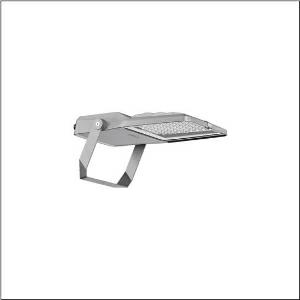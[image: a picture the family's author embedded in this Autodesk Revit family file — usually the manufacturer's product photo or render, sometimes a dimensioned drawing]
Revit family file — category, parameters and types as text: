
# Revit family: floodlight_fl_21_mini___pl64_5xa7776d2e1a_08ea
name_source: partatom
category: Lighting Fixtures
units: mm (PartAtom-declared; Revit-internal decimal feet)

## family parameters
Cut with Voids When Loaded = No
Host = Face
Light Source = No
Part Type = Normal
Room Calculation Point = No
Round Connector Dimension = Use Diameter
Shared = No

## types (1)
- --- (1 x LED, 17220 lm, 142.9 W, 3000K)
    Apparent Load = 143 VA
    CIE Flux Codes = 28 80 98 100 100
    Color Rendering = 70
    Color Temperature = 3000K
    Default Elevation = 1800 mm
    Description = Floodlight FL 21 mini, floodlight, primary light control with lens, of PMMA, primary optical cover: protective disc, of toughened safety glass, transparent, light distribution: PL64, light emission: direct distribution, installation type: surface-mounted, LED, High Power LED, rated luminous flux: 17.220lm, luminous efficacy: 121lm/W, light colour: 730, colour temperature: 3000K, control gear: Smart Interface (Zhaga), control: flexible luminous flux parameterisation, time-dependent luminous flux control, constant luminous flux control, overheat protection, pre-setting: logarithmic dimming characteristic, with terminal, 6-pole, mains connection: 220..240V, AC, 50/60Hz, start of lifetime: 143W, end of service life: 151W, reduction: 63W, luminaire housing, of diecast aluminium, powder-coated, SITECO metallic grey (DB 702S), corrosivity category C5 mid according to DIN EN ISO 12944, suitable for swimming pools, chlorine-resistant, sealing non-destructively replaceable, mounting bracket, of steel, galvanised, powder-coated, SITECO metallic grey (DB 702S), Smart Interface below and above, protection rating (complete): IP66, insulation class (complete): insulation class II (safety insulation), certification: CE, ENEC, VDE, protection symbol: D, impact resistance: IK08, permissible operating ambient temperature: -40..+40°C, permissible operating ambient temperature for outdoor applications: -40..+50°C, standard: DIN EN 12944, LABS conformity tested according to VDMA 24364:2018-05, packaging unit: 1 piece

Light Distribution: PL64
    Height = 70 mm
    Lamp = 1 x LED
    Lamp Light Flux = 17220 lm
    Lamp Power = 142.9 W
    Lamp count = 1
    Length = 485 mm
    Luminous efficacy = 121 lm/W
    Manufacturer = Siteco
    ModVariant = No
    Model = 5XA7776D2E1A
    Number of Poles = 1
    OnlyDefault = Yes
    Power Factor = 1
    Product Name = Floodlight FL 21 mini | PL64
    Product group = floodlight | pylon annexe
    ProductGroupID = 6201
    Protection Class = Protection class II
    Protection Degree = IP 66
    RLX_Detail_Level = 1
    RLX_Emergency_Light_Flux = 0 lm
    RLX_Emergency_Type = 0
    RLX_Emergency_Type_DB = No
    RlxData = <blob elided: 96301 chars, md5=d3a7c7c1>
    Socket = socket
    Standby Power = 0 W
    System Light Flux = 17220 lm
    System Power = 143 W
    Type Comments = factory setting: luminous flux: 100 % | dim-lin: 254 | 730 mA
    Type Image = l_1006845.jpg
    URL = http://relux.com
    VarID = @adj_164709
    Voltage = 0 V
    Weight = 0.00 kg
    Width = 337 mm

## geometry (parser evidence)
native form markers: Blend x4, Sweep x12
no freeform markers — native parametric forms only
